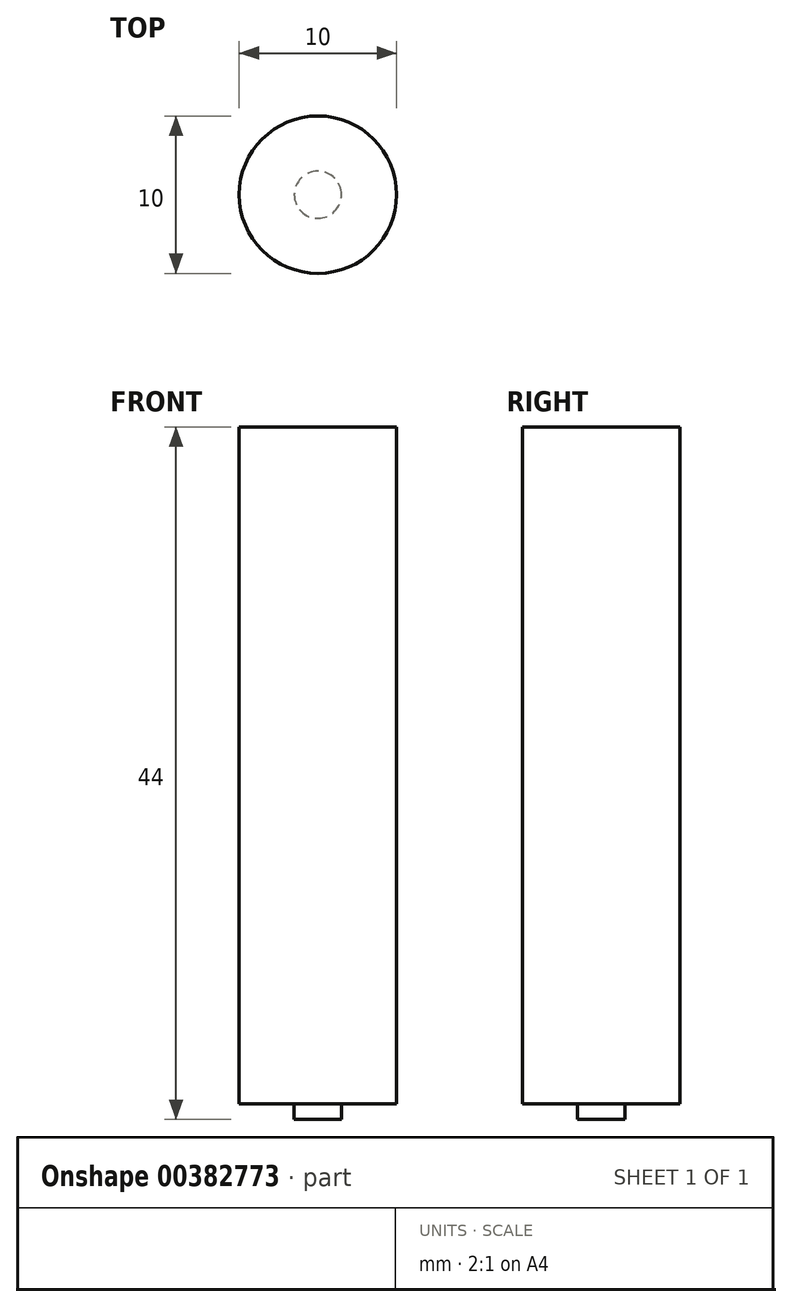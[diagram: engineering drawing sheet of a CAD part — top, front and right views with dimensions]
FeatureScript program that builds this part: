
annotation { "Feature Type Name" : "Feature", "Feature Type Description" : "" }
export const myFeature = defineFeature(function(context is Context, id is Id, definition is map)
    precondition{}
    {
        {
            var Q0;
            Q0=qCreatedBy(makeId("Top.planeOp"),FACE);
            var sketch = newSketch(context, id + "F0", { "sketchPlane" : qUnion([Q0])});
            skCircle(sketch, "E0", {"center": v(0, 0) * mm, "radius": 1.5 * mm});
            skCircle(sketch, "E1", {"center": v(0, 0) * mm, "radius": 5 * mm});
            skSolve(sketch);
        }
        {
            var Q0;
            Q0=makeQuery(id+"F0.imprint","IMPRINT",FACE,{"disambiguationData":[TD([[makeQuery(id+"F0.imprint","IMPRINT",EDGE,{"derivedFrom":sQuery(id+"F0.wireOp",EDGE,"E0")}),1.0]])]});
            extrude(context, id + "F1", {"entities" : qUnion([Q0]), "depth" : -1 * mm});
        }
        {
            var Q0;
            Q0 = qSketchRegion(id + "F0", true);
            var Q1;
            Q1=makeQuery(id+"F1.opExtrude","CAP_FACE",FACE,{"disambiguationData":[OSD([sQuery(id+"F0.wireOp",EDGE,"E0")])],"isStart":true});
            extrude(context, id + "F2", {"entities" : qUnion([Q0, Q1]), "operationType" : NewBodyOperationType.ADD, "depth" : 43 * mm});
        }
    });
